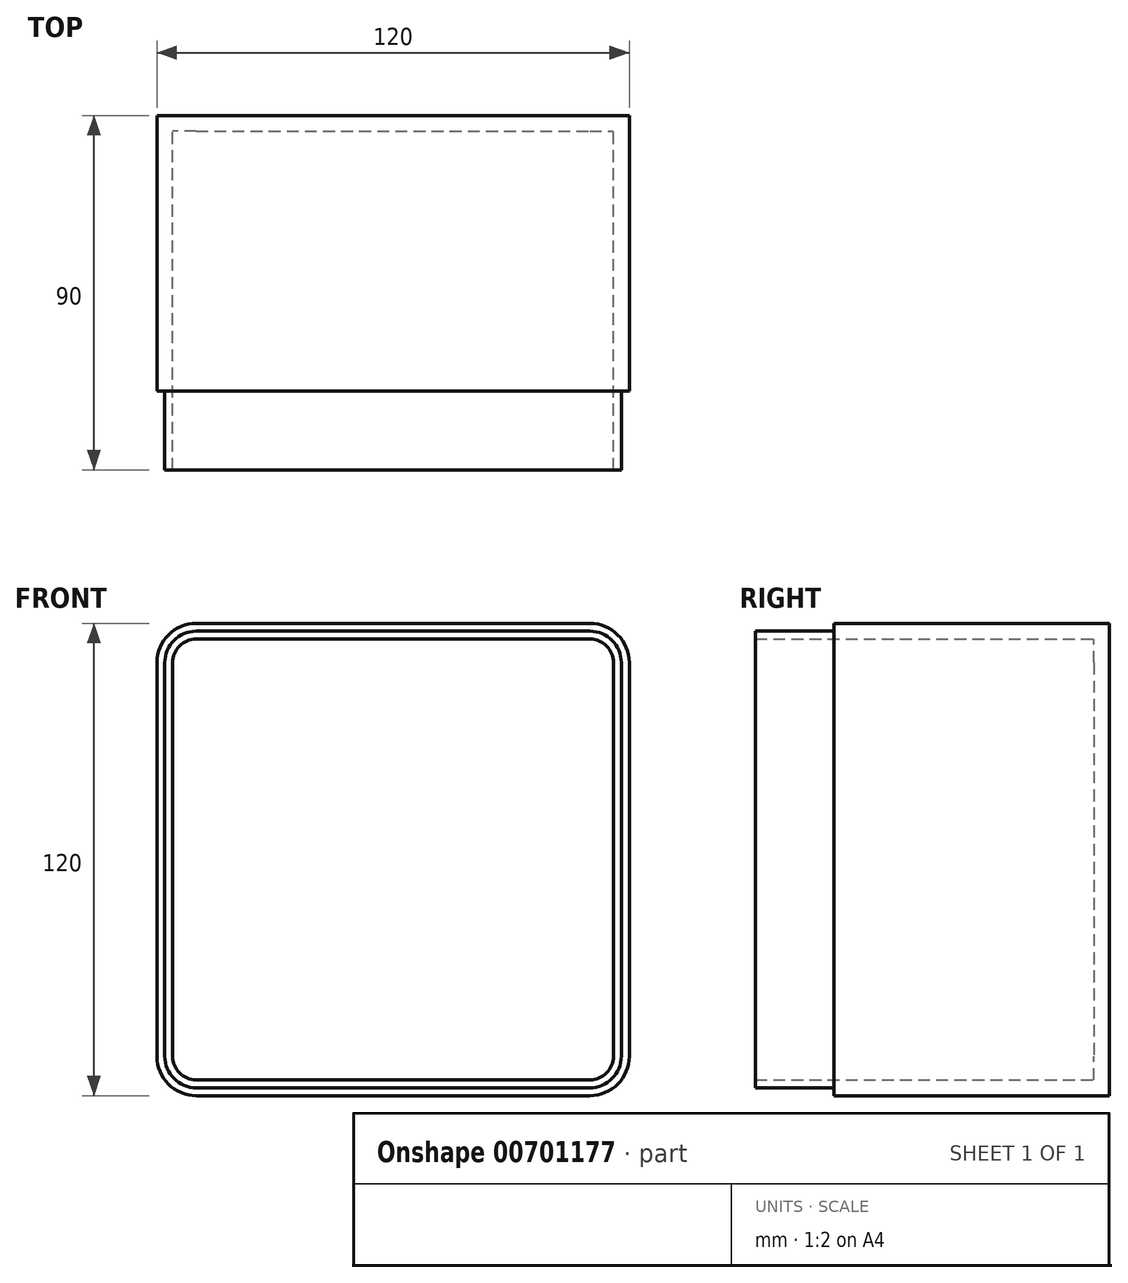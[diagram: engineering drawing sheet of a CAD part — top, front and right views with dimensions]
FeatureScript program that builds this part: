
annotation { "Feature Type Name" : "Feature", "Feature Type Description" : "" }
export const myFeature = defineFeature(function(context is Context, id is Id, definition is map)
    precondition{}
    {
        {
            var Q0;
            Q0=qCreatedBy(makeId("Front.planeOp"),FACE);
            var sketch = newSketch(context, id + "F0", { "sketchPlane" : qUnion([Q0])});
            skLineSegment(sketch, "E0.bottom", {"start": v(-48.41, 72.34) * mm, "end": v(71.59, 72.34) * mm});
            skLineSegment(sketch, "E0.top", {"start": v(-48.41, -47.66) * mm, "end": v(71.59, -47.66) * mm});
            skLineSegment(sketch, "E0.left", {"start": v(-48.41, 72.34) * mm, "end": v(-48.41, -47.66) * mm});
            skLineSegment(sketch, "E0.right", {"start": v(71.59, 72.34) * mm, "end": v(71.59, -47.66) * mm});
            skSolve(sketch);
        }
        {
            var Q0;
            Q0=makeQuery(id+"F0.imprint","IMPRINT",FACE,{"disambiguationData":[TD([[makeQuery(id+"F0.imprint","IMPRINT",EDGE,{"derivedFrom":sQuery(id+"F0.wireOp",EDGE,"E0.bottom")}),-1.0]])]});
            extrude(context, id + "F1", {"entities" : qUnion([Q0]), "depth" : 90 * mm, "offsetDistance" : 25 * mm});
        }
        {
            var Q0;
            Q0=makeQuery(id+"F1.opExtrude","SWEPT_EDGE",EDGE,{"disambiguationData":[OSD([sQuery(id+"F0.wireOp",EDGE,"E0.bottom"),sQuery(id+"F0.wireOp",EDGE,"E0.right")])]});
            var Q1;
            Q1=makeQuery(id+"F1.opExtrude","SWEPT_EDGE",EDGE,{"disambiguationData":[OSD([sQuery(id+"F0.wireOp",EDGE,"E0.bottom"),sQuery(id+"F0.wireOp",EDGE,"E0.left")])]});
            var Q2;
            Q2=makeQuery(id+"F1.opExtrude","SWEPT_EDGE",EDGE,{"disambiguationData":[OSD([sQuery(id+"F0.wireOp",EDGE,"E0.top"),sQuery(id+"F0.wireOp",EDGE,"E0.right")])]});
            var Q3;
            Q3=makeQuery(id+"F1.opExtrude","SWEPT_EDGE",EDGE,{"disambiguationData":[OSD([sQuery(id+"F0.wireOp",EDGE,"E0.top"),sQuery(id+"F0.wireOp",EDGE,"E0.left")])]});
            fillet(context, id + "F2", {"entities" : qUnion([Q0, Q1, Q2, Q3]), "radius" : 10 * mm, "tangentPropagation" : true, "allowEdgeOverflow" : false});
        }
        {
            var Q0;
            Q0=makeQuery(id+"F1.opExtrude","CAP_FACE",FACE,{"disambiguationData":[OSD([sQuery(id+"F0.wireOp",EDGE,"E0.bottom"),sQuery(id+"F0.wireOp",EDGE,"E0.top"),sQuery(id+"F0.wireOp",EDGE,"E0.left"),sQuery(id+"F0.wireOp",EDGE,"E0.right")])],"isStart":false});
            shell(context, id + "F3", {"entities" : qUnion([Q0]), "thickness" : 4 * mm});
        }
        {
            var Q0;
            Q0=makeQuery(id+"F1.opExtrude","CAP_FACE",FACE,{"disambiguationData":[OSD([sQuery(id+"F0.wireOp",EDGE,"E0.bottom"),sQuery(id+"F0.wireOp",EDGE,"E0.top"),sQuery(id+"F0.wireOp",EDGE,"E0.left"),sQuery(id+"F0.wireOp",EDGE,"E0.right")])],"isStart":false});
            var sketch = newSketch(context, id + "F4", { "sketchPlane" : qUnion([Q0])});
            skArc(sketch, "E1.0", {"start": v(-38.41, 70.34) * mm, "mid": v(-44.07, 68) * mm, "end": v(-46.41, 62.34) * mm});
            skLineSegment(sketch, "E1.1", {"start": v(61.59, 70.34) * mm, "end": v(-38.41, 70.34) * mm});
            skLineSegment(sketch, "E1.2", {"start": v(-46.41, 62.34) * mm, "end": v(-46.41, -37.66) * mm});
            skArc(sketch, "E1.3", {"start": v(69.59, 62.34) * mm, "mid": v(67.25, 68) * mm, "end": v(61.59, 70.34) * mm});
            skArc(sketch, "E1.4", {"start": v(-46.41, -37.66) * mm, "mid": v(-44.07, -43.32) * mm, "end": v(-38.41, -45.66) * mm});
            skLineSegment(sketch, "E1.5", {"start": v(-38.41, -45.66) * mm, "end": v(61.59, -45.66) * mm});
            skArc(sketch, "E1.6", {"start": v(61.59, -45.66) * mm, "mid": v(67.25, -43.32) * mm, "end": v(69.59, -37.66) * mm});
            skLineSegment(sketch, "E1.7", {"start": v(69.59, -37.66) * mm, "end": v(69.59, 62.34) * mm});
            skSolve(sketch);
        }
        {
            var Q0;
            {var subQ3=sQuery(id+"F0.wireOp",EDGE,"E0.bottom");Q0=makeQuery(id+"F4.imprint","IMPRINT",FACE,{"disambiguationData":[TD([[makeQuery(id+"F4.imprint","IMPRINT",EDGE,{"derivedFrom":makeQuery(id+"F3.opShell","OFFSET_EDGE",EDGE,{"disambiguationData":[OSD([subQ3]),TDD([makeQuery(id+"F1.opExtrude","CAP_EDGE",EDGE,{"disambiguationData":[OSD([subQ3])],"isStart":false})])]})}),-1.0]])]});}
            var Q1;
            Q1=makeQuery(id+"F4.imprint","IMPRINT",FACE,{"disambiguationData":[TD([[makeQuery(id+"F4.imprint","IMPRINT",EDGE,{"derivedFrom":sQuery(id+"F4.wireOp",EDGE,"E1.0")}),-1.0]])]});
            extrude(context, id + "F5", {"entities" : qUnion([Q0, Q1]), "operationType" : NewBodyOperationType.REMOVE, "oppositeDirection" : true, "depth" : 20 * mm, "offsetDistance" : 25 * mm});
        }
    });
